# Revit family: Приточная система с электрическом нагревателем
name_source: partatom
category: Оборудование
units: mm (PartAtom-declared; Revit-internal decimal feet)

## family parameters
Всегда вертикально = Да
Классификация = Нет
На основе рабочей плоскости = Нет
Общий = Нет
При загрузке вырезать с полостями = Нет
Размер круглого соединителя = Использовать диаметр
Тип детали = Нормальный
Точка принадлежности помещению = Нет

## types (16) — shared parameters
ADSK_Напряжение = 380 В
ADSK_Расход теплоносителя = 0.0 кубический метр в час
ADSK_Свободный напор воздуха = 400.0 Па
Длина гибкой встаки = 125 мм
Длина клапана FC = 120 мм
zero-valued in all types: Длина секции испарителя CF, Подключение испарителя E, Слив конденсата

## per-type parameters (varying)
| type | ADSK_Масса | ADSK_Номинальная мощность | ADSK_Обозначение | ADSK_Размер_Высота | ADSK_Размер_Ширина | ADSK_Частота вращения двигателя | Высота ГВ | Высота рамы | Отметка по умолчанию | Ширина ГВ |
| 1А | 241 | 23 кВт | П2.1 | 440 мм | 850 мм | 2835 | 440 мм | 0 мм | 0 мм | 850 мм |
| 2А | 280 | 41 кВт | П2.2 | 505 мм | 980 мм | 2805 | 505 мм | 0 мм | 0 мм | 980 мм |
| 16B | 1433 | 537 кВт | П2.16 | 2580 мм | 2580 мм | 1465 | 2580 мм | 120 мм | 0 мм | 2580 мм |
| 3A | 325 | 56 кВт | П2.3 | 695 мм | 1080 мм | 2830 | 695 мм | 0 мм | 6 мм | 1080 мм |
| 4A | 380 | 72 кВт | П2.4 | 695 мм | 1360 мм | 2880 | 695 мм | 0 мм | 6 мм | 1360 мм |
| 5A | 406 | 0 кВт | П2.5 | 803 мм | 1360 мм | 2880 | 803 мм | 0 мм | 0 мм | 1360 мм |
| 6A | 453 | 104 кВт | П2.6 | 803 мм | 1580 мм | 2905 | 803 мм | 0 мм | 0 мм | 1580 мм |
| 7A | 505 | 128 кВт | П2.7 | 990 мм | 1580 мм | 2945 | 990 мм | 0 мм | 0 мм | 1580 мм |
| 8A | 588 | 153 кВт | П2.8 | 990 мм | 1950 мм | 1455 | 990 мм | 0 мм | 0 мм | 1950 мм |
| 9A | 657 | 172 кВт | П2.9 | 1095 мм | 2160 мм | 1455 | 1095 мм | 0 мм | 0 мм | 2160 мм |
| 10B | 774 | 200 кВт | П2.10 | 1360 мм | 2040 мм | 1460 | 1360 мм | 0 мм | 0 мм | 2040 мм |
| 12B | 934 | 313 кВт | П2.12 | 1680 мм | 2040 мм | 1465 | 1680 мм | 120 мм | 0 мм | 2040 мм |
| 11B | 958 | 265 кВт | П2.11 | 1360 мм | 2580 мм | 1465 | 1360 мм | 0 мм | 0 мм | 2580 мм |
| 13B | 1095 | 377 кВт | П2.13 | 2040 мм | 2040 мм | 1470 | 2040 мм | 120 мм | 0 мм | 2040 мм |
| 14B | 1169 | 425 кВт | П2.14 | 1680 мм | 2580 мм | 1470 | 1680 мм | 120 мм | 0 мм | 2580 мм |
| 15B | 1260 | 457 кВт | П2.15 | 2040 мм | 2580 мм | 1470 | 2040 мм | 120 мм | 0 мм | 2580 мм |
